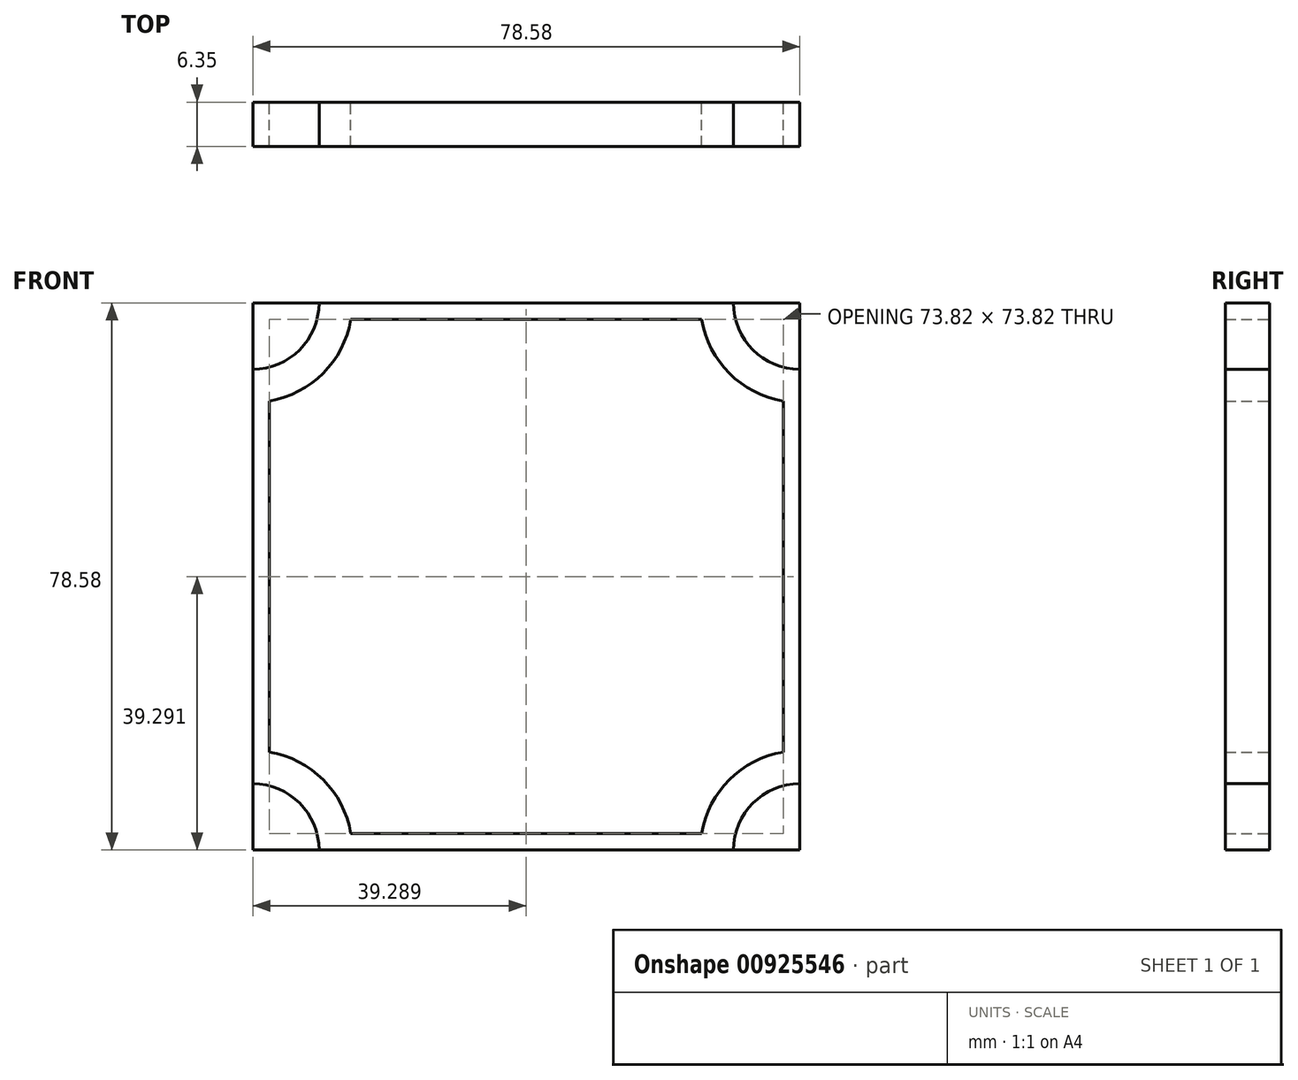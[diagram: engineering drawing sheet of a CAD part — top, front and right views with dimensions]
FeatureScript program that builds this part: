
annotation { "Feature Type Name" : "Feature", "Feature Type Description" : "" }
export const myFeature = defineFeature(function(context is Context, id is Id, definition is map)
    precondition{}
    {
        {
            var Q0;
            Q0=qCreatedBy(makeId("Front.planeOp"),FACE);
            var sketch = newSketch(context, id + "F0", { "sketchPlane" : qUnion([Q0])});
            skLineSegment(sketch, "E0.bottom", {"start": v(76.2, -76.2) * mm, "end": v(-76.2, -76.2) * mm});
            skLineSegment(sketch, "E0.top", {"start": v(76.2, 76.2) * mm, "end": v(-76.2, 76.2) * mm});
            skLineSegment(sketch, "E0.left", {"start": v(76.2, -76.2) * mm, "end": v(76.2, 76.2) * mm});
            skLineSegment(sketch, "E0.right", {"start": v(-76.2, -76.2) * mm, "end": v(-76.2, 76.2) * mm});
            skPoint(sketch, "E0.middle", {"position": v(0, 0) * mm});
            skSolve(sketch);
        }
        {
            var Q0;
            Q0=makeQuery(id+"F0.imprint","IMPRINT",FACE,{"disambiguationData":[TD([[makeQuery(id+"F0.imprint","IMPRINT",EDGE,{"derivedFrom":sQuery(id+"F0.wireOp",EDGE,"E0.bottom")}),-1.0]])]});
            var sketch = newSketch(context, id + "F1", { "sketchPlane" : qUnion([Q0])});
            skLineSegment(sketch, "E1.bottom", {"start": v(78.58, -78.58) * mm, "end": v(-78.58, -78.58) * mm});
            skLineSegment(sketch, "E1.top", {"start": v(78.58, 78.58) * mm, "end": v(-78.58, 78.58) * mm});
            skLineSegment(sketch, "E1.left", {"start": v(78.58, -78.58) * mm, "end": v(78.58, 78.58) * mm});
            skLineSegment(sketch, "E1.right", {"start": v(-78.58, -78.58) * mm, "end": v(-78.58, 78.58) * mm});
            skPoint(sketch, "E1.middle", {"position": v(0, 0) * mm});
            skLineSegment(sketch, "E2", {"start": v(-78.58, 0) * mm, "end": v(78.58, 0) * mm});
            skLineSegment(sketch, "E3", {"start": v(0, 78.58) * mm, "end": v(0, -78.58) * mm});
            skLineSegment(sketch, "E4.bottom", {"start": v(76.2, -76.2) * mm, "end": v(-76.2, -76.2) * mm});
            skLineSegment(sketch, "E4.top", {"start": v(76.2, 76.2) * mm, "end": v(-76.2, 76.2) * mm});
            skLineSegment(sketch, "E4.left", {"start": v(76.2, -76.2) * mm, "end": v(76.2, 76.2) * mm});
            skLineSegment(sketch, "E4.right", {"start": v(-76.2, -76.2) * mm, "end": v(-76.2, 76.2) * mm});
            skCircle(sketch, "E5", {"center": v(-78.58, 78.58) * mm, "radius": 9.53 * mm});
            skCircle(sketch, "E6", {"center": v(-78.58, 78.58) * mm, "radius": 14.29 * mm});
            skCircle(sketch, "E7.0.1.0", {"center": v(-78.58, 0) * mm, "radius": 14.29 * mm});
            skCircle(sketch, "E7.0.1.1", {"center": v(-78.58, 0) * mm, "radius": 9.53 * mm});
            skCircle(sketch, "E7.0.2.0", {"center": v(-78.58, -78.58) * mm, "radius": 14.29 * mm});
            skCircle(sketch, "E7.0.2.1", {"center": v(-78.58, -78.58) * mm, "radius": 9.53 * mm});
            skCircle(sketch, "E7.1.0.0", {"center": v(0, 78.58) * mm, "radius": 14.29 * mm});
            skCircle(sketch, "E7.1.0.1", {"center": v(0, 78.58) * mm, "radius": 9.53 * mm});
            skCircle(sketch, "E7.1.1.0", {"center": v(0, 0) * mm, "radius": 14.29 * mm});
            skCircle(sketch, "E7.1.1.1", {"center": v(0, 0) * mm, "radius": 9.53 * mm});
            skCircle(sketch, "E7.1.2.0", {"center": v(0, -78.58) * mm, "radius": 14.29 * mm});
            skCircle(sketch, "E7.1.2.1", {"center": v(0, -78.58) * mm, "radius": 9.53 * mm});
            skCircle(sketch, "E7.2.0.0", {"center": v(78.58, 78.58) * mm, "radius": 14.29 * mm});
            skCircle(sketch, "E7.2.0.1", {"center": v(78.58, 78.58) * mm, "radius": 9.53 * mm});
            skCircle(sketch, "E7.2.1.0", {"center": v(78.58, 0) * mm, "radius": 14.29 * mm});
            skCircle(sketch, "E7.2.1.1", {"center": v(78.58, 0) * mm, "radius": 9.53 * mm});
            skCircle(sketch, "E7.2.2.0", {"center": v(78.58, -78.58) * mm, "radius": 14.29 * mm});
            skCircle(sketch, "E7.2.2.1", {"center": v(78.58, -78.58) * mm, "radius": 9.53 * mm});
            skLineSegment(sketch, "E7.direction1", {"start": v(-78.58, 78.58) * mm, "end": v(0, 78.58) * mm, "construction": true});
            skLineSegment(sketch, "E7.direction2", {"start": v(-78.58, 78.58) * mm, "end": v(-78.58, 0) * mm, "construction": true});
            skLineSegment(sketch, "E8.0", {"start": v(-2.38, 76.2) * mm, "end": v(-2.38, -76.2) * mm});
            skLineSegment(sketch, "E9.0", {"start": v(2.38, 76.2) * mm, "end": v(2.38, -76.2) * mm});
            skLineSegment(sketch, "E10.0", {"start": v(-76.2, -2.38) * mm, "end": v(76.2, -2.38) * mm});
            skLineSegment(sketch, "E11.0", {"start": v(-76.2, 2.38) * mm, "end": v(76.2, 2.38) * mm});
            skSolve(sketch);
        }
        {
            var Q0;
            {var subQ7=sQuery(id+"F1.wireOp",EDGE,"E7.1.0.0");var subQ8=sQuery(id+"F1.wireOp",EDGE,"E4.top");var subQ9=makeQuery(id+"F1.imprint","INTERSECT",VERTEX,{"disambiguationData":[OD(1.0)],"derivedFrom":[subQ8,subQ7]});Q0=makeQuery(id+"F1.imprint","IMPRINT",FACE,{"disambiguationData":[TD([[makeQuery(id+"F1.imprint","IMPRINT",EDGE,{"disambiguationData":[TD([[subQ9,-1.0]])],"derivedFrom":subQ8}),1.0]])]});}
            extrude(context, id + "F2", {"entities" : qUnion([Q0]), "depth" : 6.35 * mm, "offsetDistance" : 30.48 * mm});
        }
        {
            var Q0;
            {var subQ0=sQuery(id+"F1.wireOp",EDGE,"E4.right");var subQ1=sQuery(id+"F1.wireOp",EDGE,"E4.top");var subQ2=makeQuery(id+"F1.imprint","INTERSECT",VERTEX,{"derivedFrom":[subQ1,subQ0]});Q0=makeQuery(id+"F1.imprint","IMPRINT",FACE,{"disambiguationData":[TD([[makeQuery(id+"F1.imprint","IMPRINT",EDGE,{"disambiguationData":[TD([[subQ2,1.0]])],"derivedFrom":subQ1}),1.0]])]});}
            var Q1;
            {var subQ0=sQuery(id+"F1.wireOp",EDGE,"E8.0");var subQ1=sQuery(id+"F1.wireOp",EDGE,"E4.top");var subQ2=makeQuery(id+"F1.imprint","INTERSECT",VERTEX,{"derivedFrom":[subQ1,subQ0]});Q1=makeQuery(id+"F1.imprint","IMPRINT",FACE,{"disambiguationData":[TD([[makeQuery(id+"F1.imprint","IMPRINT",EDGE,{"disambiguationData":[TD([[subQ2,-1.0]])],"derivedFrom":subQ1}),1.0]])]});}
            var Q2;
            {var subQ0=sQuery(id+"F1.wireOp",EDGE,"E8.0");var subQ1=sQuery(id+"F1.wireOp",EDGE,"E4.top");var subQ2=makeQuery(id+"F1.imprint","INTERSECT",VERTEX,{"derivedFrom":[subQ1,subQ0]});Q2=makeQuery(id+"F1.imprint","IMPRINT",FACE,{"disambiguationData":[TD([[makeQuery(id+"F1.imprint","IMPRINT",EDGE,{"disambiguationData":[TD([[subQ2,1.0]])],"derivedFrom":subQ1}),1.0]])]});}
            var Q3;
            {var subQ0=sQuery(id+"F1.wireOp",EDGE,"E11.0");var subQ1=sQuery(id+"F1.wireOp",EDGE,"E7.1.1.1");var subQ2=makeQuery(id+"F1.imprint","INTERSECT",VERTEX,{"disambiguationData":[OD(1.0)],"derivedFrom":[subQ1,subQ0]});Q3=makeQuery(id+"F1.imprint","IMPRINT",FACE,{"disambiguationData":[TD([[makeQuery(id+"F1.imprint","IMPRINT",EDGE,{"disambiguationData":[TD([[subQ2,-1.0]])],"derivedFrom":subQ1}),1.0]])]});}
            var Q4;
            {var subQ0=sQuery(id+"F1.wireOp",EDGE,"E8.0");var subQ1=sQuery(id+"F1.wireOp",EDGE,"E7.1.1.1");var subQ2=makeQuery(id+"F1.imprint","INTERSECT",VERTEX,{"disambiguationData":[OD(0.0)],"derivedFrom":[subQ1,subQ0]});Q4=makeQuery(id+"F1.imprint","IMPRINT",FACE,{"disambiguationData":[TD([[makeQuery(id+"F1.imprint","IMPRINT",EDGE,{"disambiguationData":[TD([[subQ2,-1.0]])],"derivedFrom":subQ1}),1.0]])]});}
            var Q5;
            {var subQ0=sQuery(id+"F1.wireOp",EDGE,"E11.0");var subQ1=sQuery(id+"F1.wireOp",EDGE,"E8.0");var subQ2=makeQuery(id+"F1.imprint","INTERSECT",VERTEX,{"derivedFrom":[subQ1,subQ0]});Q5=makeQuery(id+"F1.imprint","IMPRINT",FACE,{"disambiguationData":[TD([[makeQuery(id+"F1.imprint","IMPRINT",EDGE,{"disambiguationData":[TD([[subQ2,-1.0]])],"derivedFrom":subQ1}),1.0]])]});}
            var Q6;
            {var subQ0=sQuery(id+"F1.wireOp",EDGE,"E11.0");var subQ1=sQuery(id+"F1.wireOp",EDGE,"E4.right");var subQ2=makeQuery(id+"F1.imprint","INTERSECT",VERTEX,{"derivedFrom":[subQ1,subQ0]});Q6=makeQuery(id+"F1.imprint","IMPRINT",FACE,{"disambiguationData":[TD([[makeQuery(id+"F1.imprint","IMPRINT",EDGE,{"disambiguationData":[TD([[subQ2,-1.0]])],"derivedFrom":subQ1}),-1.0]])]});}
            var Q7;
            {var subQ4=sQuery(id+"F1.wireOp",EDGE,"E3");var subQ5=sQuery(id+"F1.wireOp",EDGE,"E1.top");var subQ6=makeQuery(id+"F1.imprint","INTERSECT",VERTEX,{"derivedFrom":[subQ5,subQ4]});Q7=makeQuery(id+"F1.imprint","IMPRINT",FACE,{"disambiguationData":[TD([[makeQuery(id+"F1.imprint","IMPRINT",EDGE,{"disambiguationData":[TD([[subQ6,-1.0]])],"derivedFrom":subQ5}),1.0]])]});}
            var Q8;
            {var subQ0=sQuery(id+"F1.wireOp",EDGE,"E7.1.1.1");var subQ1=sQuery(id+"F1.wireOp",EDGE,"E3");var subQ2=makeQuery(id+"F1.imprint","INTERSECT",VERTEX,{"disambiguationData":[OD(0.0)],"derivedFrom":[subQ1,subQ0]});Q8=makeQuery(id+"F1.imprint","IMPRINT",FACE,{"disambiguationData":[TD([[makeQuery(id+"F1.imprint","IMPRINT",EDGE,{"disambiguationData":[TD([[subQ2,-1.0]])],"derivedFrom":subQ1}),-1.0]])]});}
            var Q9;
            {var subQ0=sQuery(id+"F1.wireOp",EDGE,"E4.right");var subQ1=sQuery(id+"F1.wireOp",EDGE,"E2");var subQ2=makeQuery(id+"F1.imprint","INTERSECT",VERTEX,{"derivedFrom":[subQ1,subQ0]});Q9=makeQuery(id+"F1.imprint","IMPRINT",FACE,{"disambiguationData":[TD([[makeQuery(id+"F1.imprint","IMPRINT",EDGE,{"disambiguationData":[TD([[subQ2,-1.0]])],"derivedFrom":subQ1}),1.0]])]});}
            var Q10;
            {var subQ4=sQuery(id+"F1.wireOp",EDGE,"E1.right");var subQ6=sQuery(id+"F1.wireOp",EDGE,"E2");var subQ8=makeQuery(id+"F1.imprint","INTERSECT",VERTEX,{"derivedFrom":[subQ4,subQ6]});Q10=makeQuery(id+"F1.imprint","IMPRINT",FACE,{"disambiguationData":[TD([[makeQuery(id+"F1.imprint","IMPRINT",EDGE,{"disambiguationData":[TD([[subQ8,-1.0]])],"derivedFrom":subQ4}),-1.0]])]});}
            var Q11;
            {var subQ6=sQuery(id+"F1.wireOp",EDGE,"E1.right");var subQ7=sQuery(id+"F1.wireOp",EDGE,"E1.top");var subQ8=makeQuery(id+"F1.imprint","INTERSECT",VERTEX,{"derivedFrom":[subQ7,subQ6]});Q11=makeQuery(id+"F1.imprint","IMPRINT",FACE,{"disambiguationData":[TD([[makeQuery(id+"F1.imprint","IMPRINT",EDGE,{"disambiguationData":[TD([[subQ8,1.0]])],"derivedFrom":subQ7}),1.0]])]});}
            extrude(context, id + "F3", {"entities" : qUnion([Q0, Q1, Q2, Q3, Q4, Q5, Q6, Q7, Q8, Q9, Q10, Q11]), "depth" : 6.35 * mm, "offsetDistance" : 30.48 * mm});
        }
        {
            var Q0;
            {var subQ0=sQuery(id+"F1.wireOp",EDGE,"E6");var subQ1=sQuery(id+"F1.wireOp",EDGE,"E1.top");var subQ2=makeQuery(id+"F1.imprint","INTERSECT",VERTEX,{"derivedFrom":[subQ1,subQ0]});Q0=makeQuery(id+"F1.imprint","IMPRINT",FACE,{"disambiguationData":[TD([[makeQuery(id+"F1.imprint","IMPRINT",EDGE,{"disambiguationData":[TD([[subQ2,-1.0]])],"derivedFrom":subQ1}),1.0]])]});}
            var Q1;
            {var subQ0=sQuery(id+"F1.wireOp",EDGE,"E6");var subQ1=sQuery(id+"F1.wireOp",EDGE,"E4.top");var subQ2=makeQuery(id+"F1.imprint","INTERSECT",VERTEX,{"derivedFrom":[subQ1,subQ0]});Q1=makeQuery(id+"F1.imprint","IMPRINT",FACE,{"disambiguationData":[TD([[makeQuery(id+"F1.imprint","IMPRINT",EDGE,{"disambiguationData":[TD([[subQ2,-1.0]])],"derivedFrom":subQ1}),1.0]])]});}
            var Q2;
            {var subQ0=sQuery(id+"F1.wireOp",EDGE,"E6");var subQ1=sQuery(id+"F1.wireOp",EDGE,"E1.right");var subQ2=makeQuery(id+"F1.imprint","INTERSECT",VERTEX,{"derivedFrom":[subQ1,subQ0]});Q2=makeQuery(id+"F1.imprint","IMPRINT",FACE,{"disambiguationData":[TD([[makeQuery(id+"F1.imprint","IMPRINT",EDGE,{"disambiguationData":[TD([[subQ2,-1.0]])],"derivedFrom":subQ1}),-1.0]])]});}
            var Q3;
            {var subQ0=sQuery(id+"F1.wireOp",EDGE,"E7.0.1.0");var subQ1=sQuery(id+"F1.wireOp",EDGE,"E1.right");var subQ2=makeQuery(id+"F1.imprint","INTERSECT",VERTEX,{"disambiguationData":[OD(1.0)],"derivedFrom":[subQ1,subQ0]});Q3=makeQuery(id+"F1.imprint","IMPRINT",FACE,{"disambiguationData":[TD([[makeQuery(id+"F1.imprint","IMPRINT",EDGE,{"disambiguationData":[TD([[subQ2,-1.0]])],"derivedFrom":subQ1}),-1.0]])]});}
            var Q4;
            {var subQ0=sQuery(id+"F1.wireOp",EDGE,"E7.0.1.0");var subQ1=sQuery(id+"F1.wireOp",EDGE,"E1.right");var subQ2=makeQuery(id+"F1.imprint","INTERSECT",VERTEX,{"disambiguationData":[OD(1.0)],"derivedFrom":[subQ1,subQ0]});Q4=makeQuery(id+"F1.imprint","IMPRINT",FACE,{"disambiguationData":[TD([[makeQuery(id+"F1.imprint","IMPRINT",EDGE,{"disambiguationData":[TD([[subQ2,1.0]])],"derivedFrom":subQ1}),-1.0]])]});}
            var Q5;
            {var subQ0=sQuery(id+"F1.wireOp",EDGE,"E7.0.1.1");var subQ1=sQuery(id+"F1.wireOp",EDGE,"E4.right");var subQ2=makeQuery(id+"F1.imprint","INTERSECT",VERTEX,{"disambiguationData":[OD(1.0)],"derivedFrom":[subQ1,subQ0]});Q5=makeQuery(id+"F1.imprint","IMPRINT",FACE,{"disambiguationData":[TD([[makeQuery(id+"F1.imprint","IMPRINT",EDGE,{"disambiguationData":[TD([[subQ2,-1.0]])],"derivedFrom":subQ1}),-1.0]])]});}
            var Q6;
            {var subQ0=sQuery(id+"F1.wireOp",EDGE,"E11.0");var subQ1=sQuery(id+"F1.wireOp",EDGE,"E7.0.1.0");var subQ2=makeQuery(id+"F1.imprint","INTERSECT",VERTEX,{"derivedFrom":[subQ1,subQ0]});Q6=makeQuery(id+"F1.imprint","IMPRINT",FACE,{"disambiguationData":[TD([[makeQuery(id+"F1.imprint","IMPRINT",EDGE,{"disambiguationData":[TD([[subQ2,1.0]])],"derivedFrom":subQ1}),1.0]])]});}
            var Q7;
            {var subQ0=sQuery(id+"F1.wireOp",EDGE,"E11.0");var subQ1=sQuery(id+"F1.wireOp",EDGE,"E7.0.1.0");var subQ2=makeQuery(id+"F1.imprint","INTERSECT",VERTEX,{"derivedFrom":[subQ1,subQ0]});Q7=makeQuery(id+"F1.imprint","IMPRINT",FACE,{"disambiguationData":[TD([[makeQuery(id+"F1.imprint","IMPRINT",EDGE,{"disambiguationData":[TD([[subQ2,1.0]])],"derivedFrom":subQ1}),-1.0]])]});}
            var Q8;
            {var subQ0=sQuery(id+"F1.wireOp",EDGE,"E8.0");var subQ1=sQuery(id+"F1.wireOp",EDGE,"E7.1.1.0");var subQ2=makeQuery(id+"F1.imprint","INTERSECT",VERTEX,{"disambiguationData":[OD(0.0)],"derivedFrom":[subQ1,subQ0]});Q8=makeQuery(id+"F1.imprint","IMPRINT",FACE,{"disambiguationData":[TD([[makeQuery(id+"F1.imprint","IMPRINT",EDGE,{"disambiguationData":[TD([[subQ2,-1.0]])],"derivedFrom":subQ1}),1.0]])]});}
            var Q9;
            {var subQ0=sQuery(id+"F1.wireOp",EDGE,"E11.0");var subQ1=sQuery(id+"F1.wireOp",EDGE,"E7.1.1.0");var subQ2=makeQuery(id+"F1.imprint","INTERSECT",VERTEX,{"disambiguationData":[OD(1.0)],"derivedFrom":[subQ1,subQ0]});Q9=makeQuery(id+"F1.imprint","IMPRINT",FACE,{"disambiguationData":[TD([[makeQuery(id+"F1.imprint","IMPRINT",EDGE,{"disambiguationData":[TD([[subQ2,-1.0]])],"derivedFrom":subQ1}),1.0]])]});}
            var Q10;
            {var subQ0=sQuery(id+"F1.wireOp",EDGE,"E8.0");var subQ1=sQuery(id+"F1.wireOp",EDGE,"E7.1.0.0");var subQ2=makeQuery(id+"F1.imprint","INTERSECT",VERTEX,{"derivedFrom":[subQ1,subQ0]});Q10=makeQuery(id+"F1.imprint","IMPRINT",FACE,{"disambiguationData":[TD([[makeQuery(id+"F1.imprint","IMPRINT",EDGE,{"disambiguationData":[TD([[subQ2,-1.0]])],"derivedFrom":subQ1}),-1.0]])]});}
            var Q11;
            {var subQ0=sQuery(id+"F1.wireOp",EDGE,"E7.1.0.1");var subQ1=sQuery(id+"F1.wireOp",EDGE,"E4.top");var subQ2=makeQuery(id+"F1.imprint","INTERSECT",VERTEX,{"disambiguationData":[OD(1.0)],"derivedFrom":[subQ1,subQ0]});Q11=makeQuery(id+"F1.imprint","IMPRINT",FACE,{"disambiguationData":[TD([[makeQuery(id+"F1.imprint","IMPRINT",EDGE,{"disambiguationData":[TD([[subQ2,-1.0]])],"derivedFrom":subQ1}),1.0]])]});}
            var Q12;
            {var subQ0=sQuery(id+"F1.wireOp",EDGE,"E8.0");var subQ1=sQuery(id+"F1.wireOp",EDGE,"E7.1.0.0");var subQ2=makeQuery(id+"F1.imprint","INTERSECT",VERTEX,{"derivedFrom":[subQ1,subQ0]});Q12=makeQuery(id+"F1.imprint","IMPRINT",FACE,{"disambiguationData":[TD([[makeQuery(id+"F1.imprint","IMPRINT",EDGE,{"disambiguationData":[TD([[subQ2,-1.0]])],"derivedFrom":subQ1}),1.0]])]});}
            var Q13;
            {var subQ0=sQuery(id+"F1.wireOp",EDGE,"E7.1.0.0");var subQ1=sQuery(id+"F1.wireOp",EDGE,"E1.top");var subQ2=makeQuery(id+"F1.imprint","INTERSECT",VERTEX,{"disambiguationData":[OD(1.0)],"derivedFrom":[subQ1,subQ0]});Q13=makeQuery(id+"F1.imprint","IMPRINT",FACE,{"disambiguationData":[TD([[makeQuery(id+"F1.imprint","IMPRINT",EDGE,{"disambiguationData":[TD([[subQ2,1.0]])],"derivedFrom":subQ1}),1.0]])]});}
            var Q14;
            {var subQ0=sQuery(id+"F1.wireOp",EDGE,"E7.1.0.0");var subQ1=sQuery(id+"F1.wireOp",EDGE,"E1.top");var subQ2=makeQuery(id+"F1.imprint","INTERSECT",VERTEX,{"disambiguationData":[OD(1.0)],"derivedFrom":[subQ1,subQ0]});Q14=makeQuery(id+"F1.imprint","IMPRINT",FACE,{"disambiguationData":[TD([[makeQuery(id+"F1.imprint","IMPRINT",EDGE,{"disambiguationData":[TD([[subQ2,-1.0]])],"derivedFrom":subQ1}),1.0]])]});}
            var Q15;
            {var subQ0=sQuery(id+"F1.wireOp",EDGE,"E7.1.1.0");var subQ1=sQuery(id+"F1.wireOp",EDGE,"E3");var subQ2=makeQuery(id+"F1.imprint","INTERSECT",VERTEX,{"disambiguationData":[OD(0.0)],"derivedFrom":[subQ1,subQ0]});Q15=makeQuery(id+"F1.imprint","IMPRINT",FACE,{"disambiguationData":[TD([[makeQuery(id+"F1.imprint","IMPRINT",EDGE,{"disambiguationData":[TD([[subQ2,-1.0]])],"derivedFrom":subQ1}),-1.0]])]});}
            extrude(context, id + "F4", {"entities" : qUnion([Q0, Q1, Q2, Q3, Q4, Q5, Q6, Q7, Q8, Q9, Q10, Q11, Q12, Q13, Q14, Q15]), "depth" : 6.35 * mm, "offsetDistance" : 30.48 * mm});
        }
    });
